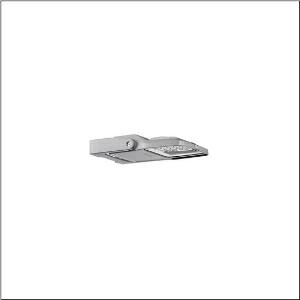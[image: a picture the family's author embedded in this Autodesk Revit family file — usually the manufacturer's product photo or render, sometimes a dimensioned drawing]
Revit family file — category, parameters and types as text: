
# Revit family: floodlight_fl_21_iq_micro___pl64_5xa7762a4e2a_da81
name_source: partatom
category: Lighting Fixtures
units: mm (PartAtom-declared; Revit-internal decimal feet)

## family parameters
Cut with Voids When Loaded = No
Host = Face
Light Source = No
Part Type = Normal
Room Calculation Point = No
Round Connector Dimension = Use Diameter
Shared = No

## types (1)
- --- (1 x LED, 2980 lm, 23.1 W, 4000K)
    Apparent Load = 23 VA
    CIE Flux Codes = 28 80 98 100 100
    Color Rendering = 70
    Color Temperature = 4000K
    Default Elevation = 1800 mm
    Description = Floodlight FL 21 iQ micro, floodlight, primary light control with lens, of PMMA, primary optical cover: protective disc, of toughened safety glass, transparent, light distribution: PL64, light emission: direct distribution, installation type: surface-mounted, lamps: LED, High Power LED, rated values: 2.980lm | 23,1W | 129lm/W (begin service life); end service life: 2.980lm | 23,8W; at 50% lumin. flux: 1.490lm | 11W | 135,5lm/W, colour temperature: 4000K, colour rendering: CRI > 70, light colour: 740, light setting 1 begin service life: 100% | 2.980lm | 23,1W | 129lm/W | 4.000K, light setting 1 end service life: 23,8W, further light settings possible, control: Auto-Match, Temp-Guard, Night-Set, Smart-Wire, Desk-Remote (wireless, voltage-free reading and setting of iQ features in the workshop via application-optimized NFC function/RFID function), optimised constant luminous flux control (CLO 2.0), Street-Remote, pre-setting: linear dimming characteristic, with terminal, 6-pole, mains connection: 220..240V, AC, 50/60Hz, luminaire housing, of diecast aluminium, powder-coated, SITECO metallic grey (DB 702S), corrosivity category C5 mid according to DIN EN ISO 12944suitable for swimming poolschlorine-resistant, sealing non-destructively replaceable, design bracket, of diecast aluminium, powder-coated, SITECO metallic grey (DB 702S), protection rating (complete): IP66, insulation class (complete): insulation class II (safety insulation), certification: CE, ENEC, VDE, protection symbol: D, impact resistance: IK07, permissible operating ambient temperature: -40..+40°C, permissible operating ambient temperature for outdoor applications: -40..+50°C, standard: DIN EN 12944, LABS conformity tested according to VDMA 24364:2018-05, packaging unit: 1 piece

Light Distribution: PL64
    Height = 65 mm
    Lamp = 1 x LED
    Lamp Light Flux = 2980 lm
    Lamp Power = 23.1 W
    Lamp count = 1
    Length = 312 mm
    Luminous efficacy = 129 lm/W
    Manufacturer = Siteco
    ModVariant = No
    Model = 5XA7762A4E2A
    Mounting Place = Wall
    Mounting Type = Surface mounted
    Number of Poles = 1
    OnlyDefault = Yes
    Power Factor = 1
    Product Name = Floodlight FL 21 iQ micro | PL64
    Product group = floodlight | wall mounted
    ProductGroupID = 2002
    Protection Class = Protection class II
    Protection Degree = IP 66
    RLX_Detail_Level = 1
    RLX_Emergency_Light_Flux = 0 lm
    RLX_Emergency_Type = 0
    RLX_Emergency_Type_DB = No
    RlxData = <blob elided: 97593 chars, md5=f9353180>
    Socket = socket
    Standby Power = 0 W
    System Light Flux = 2980 lm
    System Power = 23 W
    Type Comments = factory setting: luminous flux: 100 % | dim-lin: 254 | 455 mA
    Type Image = l_1006878.jpg
    URL = http://relux.com
    VarID = @adj_180829
    Voltage = 0 V
    Weight = 0.00 kg
    Width = 230 mm

## geometry (parser evidence)
native form markers: Blend x4, Sweep x13
no freeform markers — native parametric forms only
